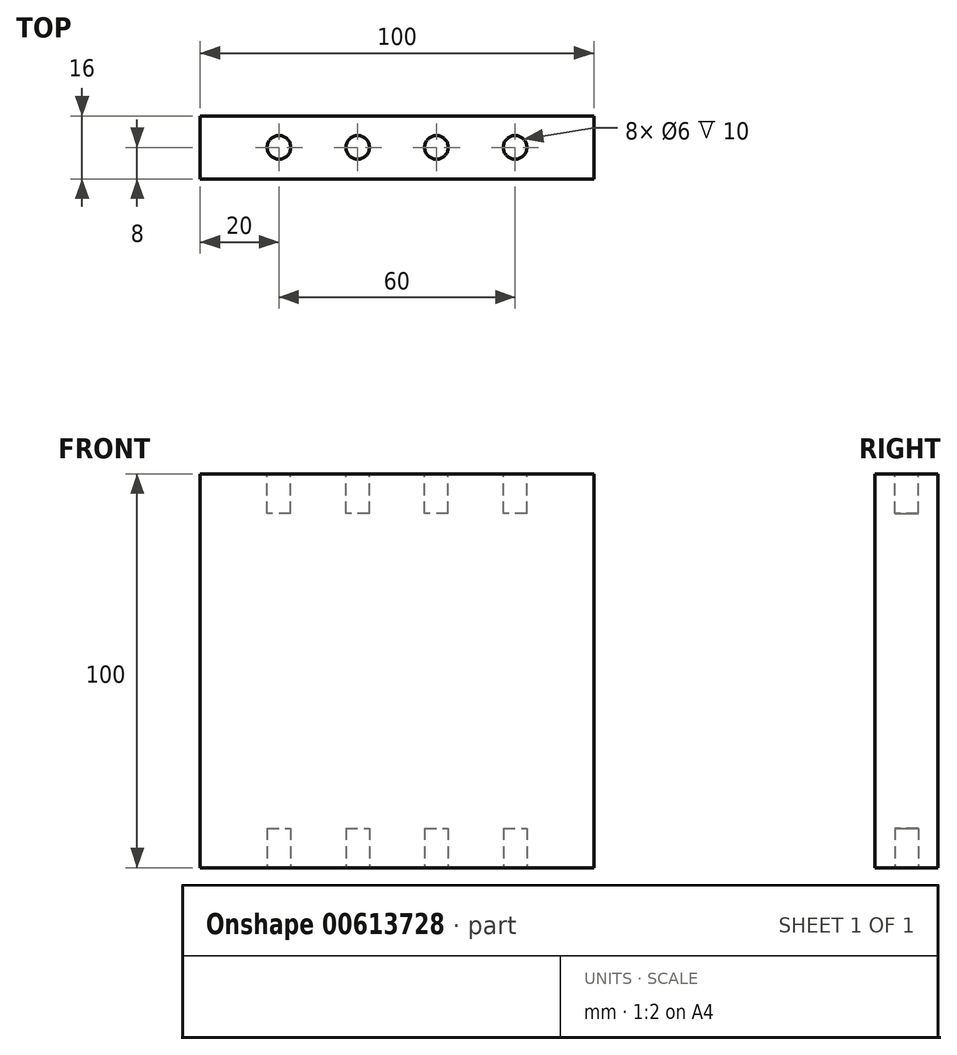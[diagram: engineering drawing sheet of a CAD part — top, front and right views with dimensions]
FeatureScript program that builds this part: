
annotation { "Feature Type Name" : "Feature", "Feature Type Description" : "" }
export const myFeature = defineFeature(function(context is Context, id is Id, definition is map)
    precondition{}
    {
        {
            var Q0;
            Q0=qCreatedBy(makeId("Front.planeOp"),FACE);
            var sketch = newSketch(context, id + "F0", { "sketchPlane" : qUnion([Q0])});
            skLineSegment(sketch, "E0.bottom", {"start": v(50, 50) * mm, "end": v(-50, 50) * mm});
            skLineSegment(sketch, "E0.top", {"start": v(50, -50) * mm, "end": v(-50, -50) * mm});
            skLineSegment(sketch, "E0.left", {"start": v(50, 50) * mm, "end": v(50, -50) * mm});
            skLineSegment(sketch, "E0.right", {"start": v(-50, 50) * mm, "end": v(-50, -50) * mm});
            skPoint(sketch, "E0.middle", {"position": v(0, 0) * mm});
            skSolve(sketch);
        }
        {
            var Q0;
            Q0=qSketchRegion(id+"F0",true);
            extrude(context, id + "F1", {"entities" : qUnion([Q0]), "depth" : 16 * mm, "offsetDistance" : 25 * mm});
        }
        {
            var Q0;
            Q0=makeQuery(id+"F1.opExtrude","SWEPT_FACE",FACE,{"disambiguationData":[OSD([sQuery(id+"F0.wireOp",EDGE,"E0.bottom")])]});
            var sketch = newSketch(context, id + "F2", { "sketchPlane" : qUnion([Q0])});
            skCircle(sketch, "E1", {"center": v(-30, -8) * mm, "radius": 3 * mm});
            skCircle(sketch, "E2", {"center": v(-10, -8) * mm, "radius": 3 * mm});
            skCircle(sketch, "E3", {"center": v(10, -8) * mm, "radius": 3 * mm});
            skCircle(sketch, "E4", {"center": v(30, -8) * mm, "radius": 3 * mm});
            skLineSegment(sketch, "E5", {"start": v(-30, -8) * mm, "end": v(-10, -8) * mm, "construction": true});
            skLineSegment(sketch, "E6", {"start": v(10, -8) * mm, "end": v(30, -8) * mm, "construction": true});
            skLineSegment(sketch, "E7", {"start": v(30, -8) * mm, "end": v(50, -8) * mm, "construction": true});
            skLineSegment(sketch, "E8", {"start": v(0, 0) * mm, "end": v(0, -8) * mm, "construction": true});
            skLineSegment(sketch, "E9", {"start": v(0, -8) * mm, "end": v(0, -16) * mm, "construction": true});
            skLineSegment(sketch, "E10", {"start": v(-50, -8) * mm, "end": v(-30, -8) * mm, "construction": true});
            skLineSegment(sketch, "E11", {"start": v(-10, -8) * mm, "end": v(10, -8) * mm, "construction": true});
            skSolve(sketch);
        }
        {
            var Q0;
            Q0=qSketchRegion(id+"F2",true);
            extrude(context, id + "F3", {"entities" : qUnion([Q0]), "operationType" : NewBodyOperationType.REMOVE, "oppositeDirection" : true, "depth" : 10 * mm, "offsetDistance" : 25 * mm});
        }
        {
            var Q0;
            Q0=makeQuery(id+"F1.opExtrude","SWEPT_FACE",FACE,{"disambiguationData":[OSD([sQuery(id+"F0.wireOp",EDGE,"E0.top")])]});
            var sketch = newSketch(context, id + "F4", { "sketchPlane" : qUnion([Q0])});
            skCircle(sketch, "E12", {"center": v(-10, 8) * mm, "radius": 3 * mm});
            skCircle(sketch, "E13", {"center": v(-30, 8) * mm, "radius": 3 * mm});
            skCircle(sketch, "E14", {"center": v(10, 8) * mm, "radius": 3 * mm});
            skCircle(sketch, "E15", {"center": v(30, 8) * mm, "radius": 3 * mm});
            skLineSegment(sketch, "E16", {"start": v(-50, 8) * mm, "end": v(-30, 8) * mm, "construction": true});
            skLineSegment(sketch, "E17", {"start": v(-10, 8) * mm, "end": v(10, 8) * mm, "construction": true});
            skLineSegment(sketch, "E18", {"start": v(30, 8) * mm, "end": v(50, 8) * mm, "construction": true});
            skLineSegment(sketch, "E19", {"start": v(-30, 8) * mm, "end": v(-10, 8) * mm, "construction": true});
            skLineSegment(sketch, "E20", {"start": v(10, 8) * mm, "end": v(30, 8) * mm, "construction": true});
            skSolve(sketch);
        }
        {
            var Q0;
            Q0=qSketchRegion(id+"F4",true);
            extrude(context, id + "F5", {"entities" : qUnion([Q0]), "operationType" : NewBodyOperationType.REMOVE, "oppositeDirection" : true, "depth" : 10 * mm, "offsetDistance" : 25 * mm});
        }
    });
